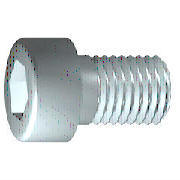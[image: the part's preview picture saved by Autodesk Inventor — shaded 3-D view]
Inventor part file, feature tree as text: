
AUTODESK INVENTOR PART (.ipt)
format: ipt  version: 2017 (Build 210142000, 142)  size: 183,808 bytes
history: native  units: mm (DEFAULTED — no unit token found)
features: sketch x2, extrude x1, plane x1, fillet x1
ambient origin geometry x7: Origin, YZ Plane, XY Plane, X Axis, Y Axis, Z Axis, Center Point
bodies: Solid1 (feature_tree), Body (feature_tree)
feature tree (5):
  extrude  "Slot"  Depth=3.0mm
  plane  "Work Plane1"
  fillet  "Fillet2"  Radius=3.0mm
  sketch  "Sketch1"  dims[d1=18.0mm d2=0.306825mm d3=3.0mm]
  sketch  "Sketch2"  dims[d4=1.5mm d5=60.0deg d6=3.0mm d7=3.0mm d8=2.886751mm d9=5.5mm d10=90.0deg d11=10.0mm d12=0.0mm d13=18.0mm d14=0.0mm d15=0.306725mm d16=0.306725mm d17=0.3mm d19=0.0mm d26=30.0mm d27=45.0deg d28=0.0mm d29=0.0mm d30=0.1mm]
